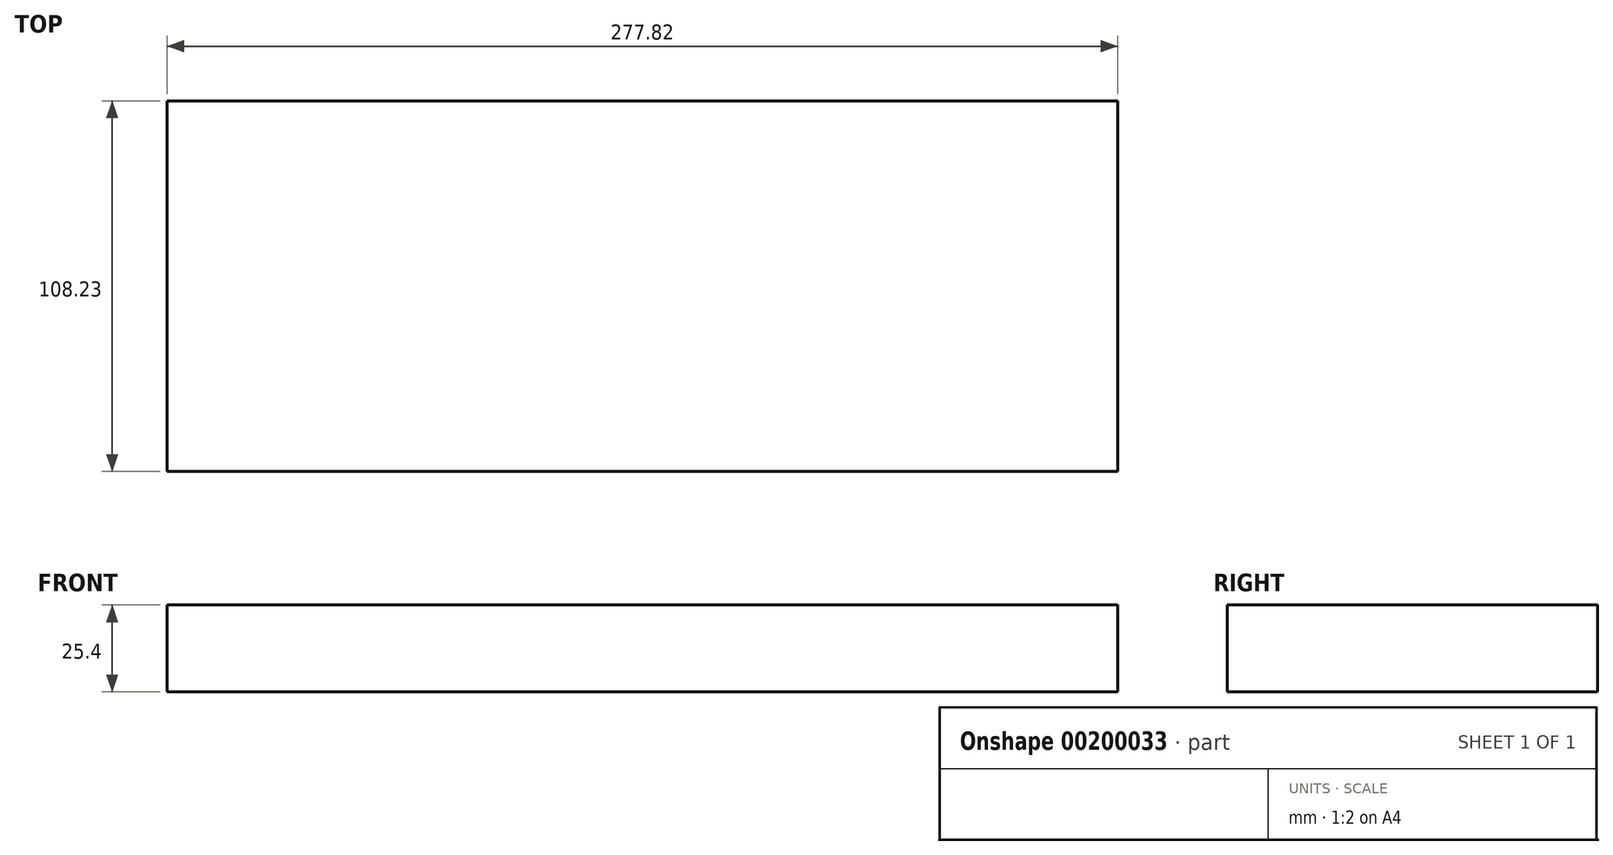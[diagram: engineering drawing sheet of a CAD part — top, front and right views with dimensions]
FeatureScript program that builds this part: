
annotation { "Feature Type Name" : "Feature", "Feature Type Description" : "" }
export const myFeature = defineFeature(function(context is Context, id is Id, definition is map)
    precondition{}
    {
        {
            var Q0;
            Q0=qCreatedBy(makeId("Top.planeOp"),FACE);
            var sketch = newSketch(context, id + "F0", { "sketchPlane" : qUnion([Q0])});
            skLineSegment(sketch, "E0.bottom", {"start": v(-110.32, 35.98) * mm, "end": v(167.5, 35.98) * mm});
            skLineSegment(sketch, "E0.top", {"start": v(-110.32, -72.25) * mm, "end": v(167.5, -72.25) * mm});
            skLineSegment(sketch, "E0.left", {"start": v(-110.32, 35.98) * mm, "end": v(-110.32, -72.25) * mm});
            skLineSegment(sketch, "E0.right", {"start": v(167.5, 35.98) * mm, "end": v(167.5, -72.25) * mm});
            skSolve(sketch);
        }
        {
            var Q0;
            Q0=makeQuery(id+"F0.imprint","IMPRINT",FACE,{"disambiguationData":[TD([[makeQuery(id+"F0.imprint","IMPRINT",EDGE,{"derivedFrom":sQuery(id+"F0.wireOp",EDGE,"E0.bottom")}),-1.0]])]});
            extrude(context, id + "F1", {"entities" : qUnion([Q0]), "depth" : 25.4 * mm});
        }
    });
